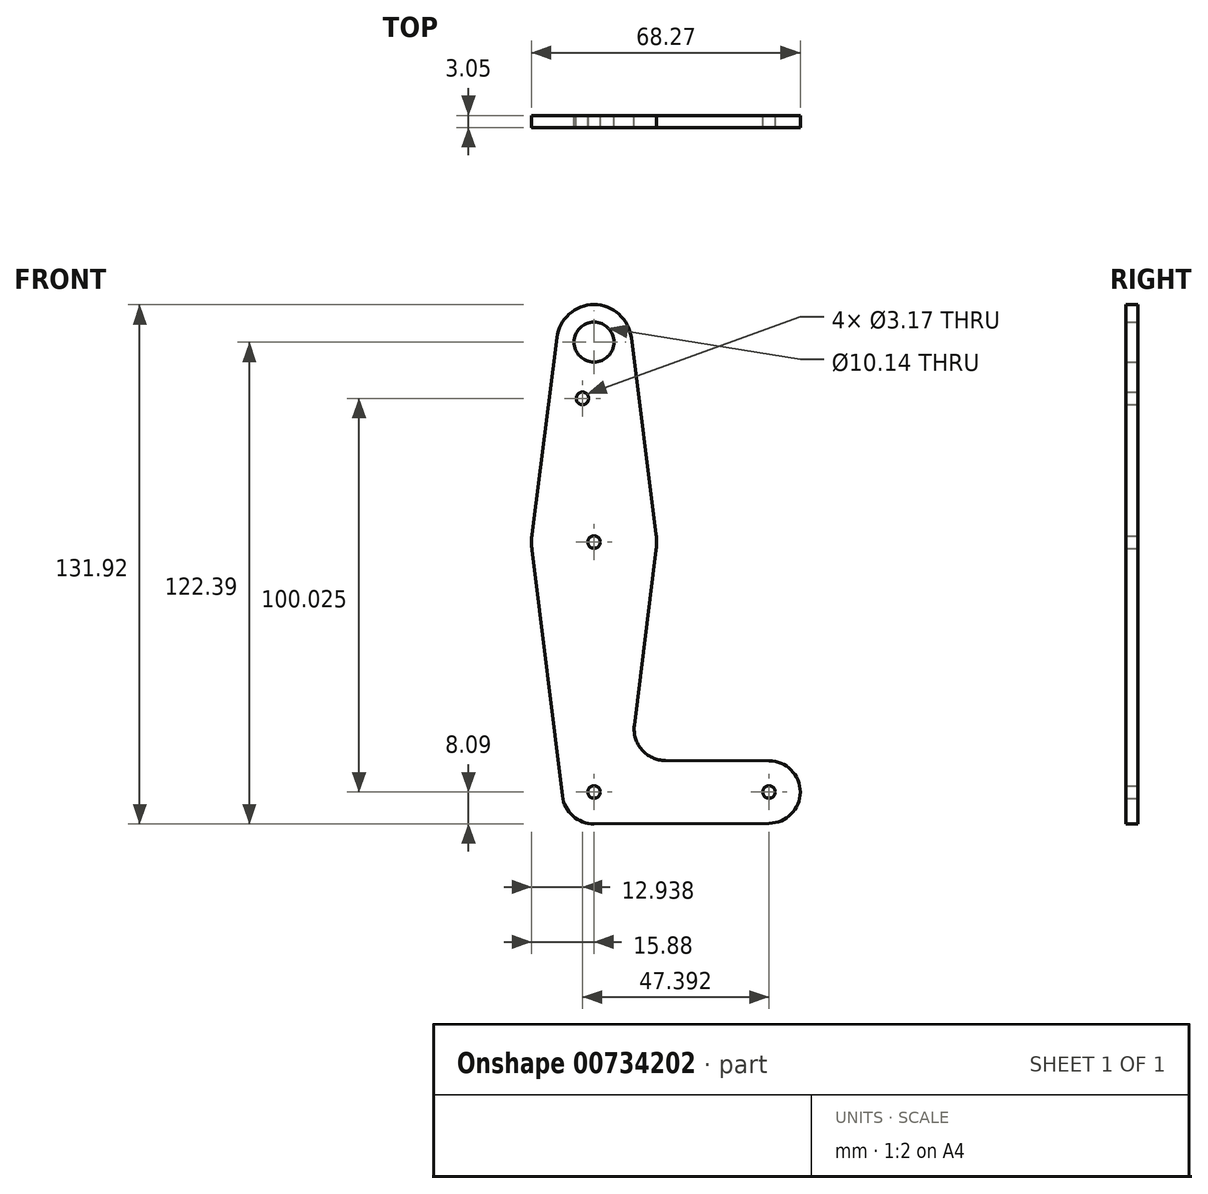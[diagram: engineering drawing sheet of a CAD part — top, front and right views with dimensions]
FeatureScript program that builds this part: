
annotation { "Feature Type Name" : "Feature", "Feature Type Description" : "" }
export const myFeature = defineFeature(function(context is Context, id is Id, definition is map)
    precondition{}
    {
        {
            var Q0;
            Q0=qCreatedBy(makeId("Front.planeOp"),FACE);
            var sketch = newSketch(context, id + "F0", { "sketchPlane" : qUnion([Q0])});
            skLineSegment(sketch, "E0", {"start": v(0, 0) * mm, "end": v(0, 114.3) * mm, "construction": true});
            skLineSegment(sketch, "E1", {"start": v(0, 0) * mm, "end": v(44.45, 0) * mm, "construction": true});
            skCircle(sketch, "E2", {"center": v(0, 114.3) * mm, "radius": 9.53 * mm});
            skCircle(sketch, "E3", {"center": v(44.45, 0) * mm, "radius": 7.94 * mm});
            skCircle(sketch, "E4", {"center": v(0, 63.5) * mm, "radius": 15.88 * mm});
            skLineSegment(sketch, "E5", {"start": v(-9.45, 115.5) * mm, "end": v(-15.75, 65.48) * mm});
            skLineSegment(sketch, "E6", {"start": v(9.45, 115.5) * mm, "end": v(15.75, 65.48) * mm});
            skCircle(sketch, "E7", {"center": v(-2.94, 100.03) * mm, "radius": 1.59 * mm});
            skCircle(sketch, "E8", {"center": v(0, 114.3) * mm, "radius": 5.07 * mm});
            skCircle(sketch, "E9", {"center": v(0, 63.5) * mm, "radius": 1.59 * mm});
            skCircle(sketch, "E10", {"center": v(0, 0) * mm, "radius": 1.59 * mm});
            skCircle(sketch, "E11", {"center": v(44.45, 0) * mm, "radius": 1.59 * mm});
            skPoint(sketch, "E12.start.orphan", {"position": v(0, -8.09) * mm});
            skPoint(sketch, "E13.end.orphan", {"position": v(-8.16, 0) * mm});
            skLineSegment(sketch, "E14", {"start": v(8.15, -0.02) * mm, "end": v(8.1, 0.04) * mm});
            skPoint(sketch, "E15.newPointA", {"position": v(0, 8.09) * mm});
            skArc(sketch, "E16.trimOffspring", {"start": v(8.1, 0) * mm, "mid": v(8.1, 0.02) * mm, "end": v(8.1, 0.04) * mm});
            skCircle(sketch, "E17", {"center": v(0, 0) * mm, "radius": 8.09 * mm});
            skLineSegment(sketch, "E18", {"start": v(8.15, 0) * mm, "end": v(8.15, -0.02) * mm});
            skLineSegment(sketch, "E19", {"start": v(-15.76, 61.55) * mm, "end": v(-8.03, -1) * mm});
            skLineSegment(sketch, "E20", {"start": v(15.76, 61.55) * mm, "end": v(10.25, 16.95) * mm});
            skLineSegment(sketch, "E21", {"start": v(18.1, 8.03) * mm, "end": v(44.48, 7.94) * mm});
            skLineSegment(sketch, "E22", {"start": v(0, -8.09) * mm, "end": v(44.48, -7.94) * mm});
            skArc(sketch, "E23.filletArc", {"start": v(10.25, 16.95) * mm, "mid": v(12.17, 10.72) * mm, "end": v(18.1, 8.03) * mm});
            skSolve(sketch);
        }
        {
            var Q0;
            Q0 = qSketchRegion(id + "F0", true);
            extrude(context, id + "F1", {"entities" : qUnion([Q0]), "depth" : 3.05 * mm, "offsetDistance" : 25.4 * mm});
        }
    });
